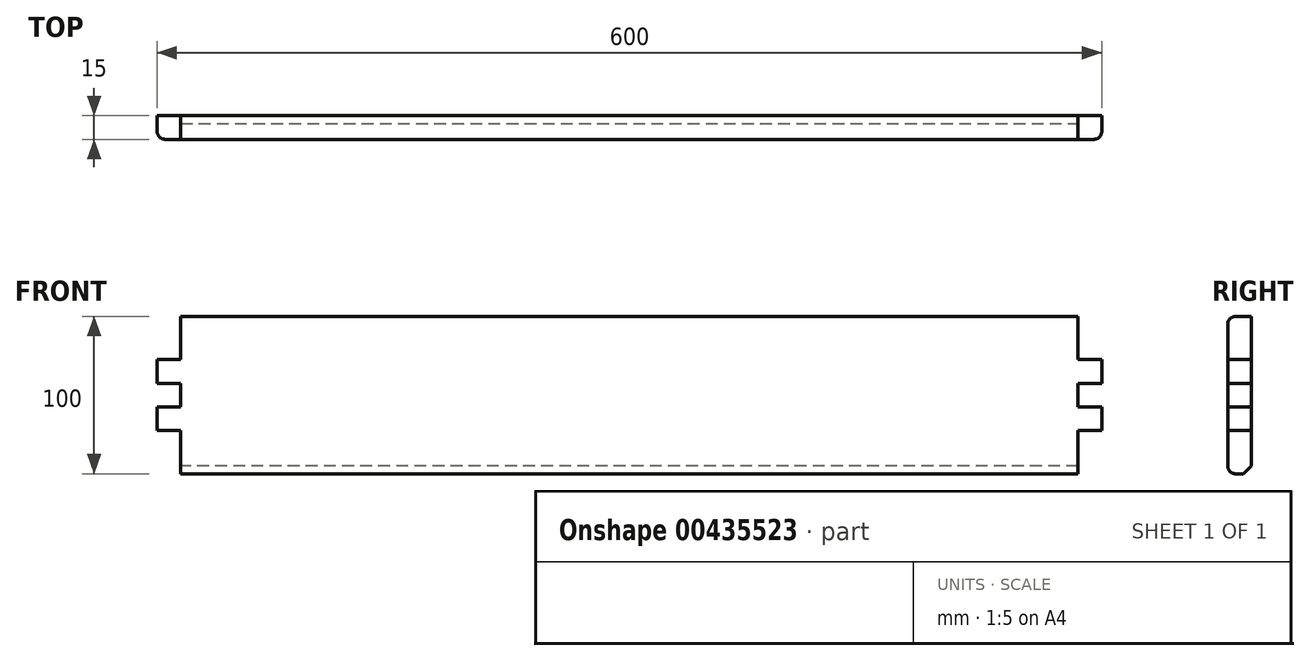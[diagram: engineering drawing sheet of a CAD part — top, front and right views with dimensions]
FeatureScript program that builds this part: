
annotation { "Feature Type Name" : "Feature", "Feature Type Description" : "" }
export const myFeature = defineFeature(function(context is Context, id is Id, definition is map)
    precondition{}
    {
        {
            var Q0;
            Q0=qCreatedBy(makeId("Front.planeOp"),FACE);
            var sketch = newSketch(context, id + "F0", { "sketchPlane" : qUnion([Q0])});
            skPoint(sketch, "E0.middle", {"position": v(0, 0) * mm});
            skLineSegment(sketch, "E1", {"start": v(-285, -22.5) * mm, "end": v(-300, -22.5) * mm});
            skLineSegment(sketch, "E2", {"start": v(-300, -22.5) * mm, "end": v(-300, -7.5) * mm});
            skLineSegment(sketch, "E3", {"start": v(-300, -7.5) * mm, "end": v(-285, -7.5) * mm});
            skLineSegment(sketch, "E4", {"start": v(-285, 7.5) * mm, "end": v(-300, 7.5) * mm});
            skLineSegment(sketch, "E5", {"start": v(-300, 7.5) * mm, "end": v(-300, 22.5) * mm});
            skLineSegment(sketch, "E6", {"start": v(-300, 22.5) * mm, "end": v(-285, 22.5) * mm});
            skLineSegment(sketch, "E7", {"start": v(-285, 50) * mm, "end": v(-285, 22.5) * mm});
            skLineSegment(sketch, "E8", {"start": v(-285, 7.5) * mm, "end": v(-285, -7.5) * mm});
            skLineSegment(sketch, "E9", {"start": v(-285, -22.5) * mm, "end": v(-285, -50) * mm});
            skLineSegment(sketch, "E10", {"start": v(-285, 50) * mm, "end": v(0, 50) * mm});
            skLineSegment(sketch, "E11", {"start": v(0, -50) * mm, "end": v(-285, -50) * mm});
            skLineSegment(sketch, "E12.MirrorCS", {"start": v(285, 7.5) * mm, "end": v(300, 7.5) * mm});
            skLineSegment(sketch, "E13.MirrorCS", {"start": v(300, -7.5) * mm, "end": v(285, -7.5) * mm});
            skLineSegment(sketch, "E14.MirrorCS", {"start": v(285, -22.5) * mm, "end": v(300, -22.5) * mm});
            skLineSegment(sketch, "E15.MirrorCS", {"start": v(300, 7.5) * mm, "end": v(300, 22.5) * mm});
            skLineSegment(sketch, "E16.MirrorCS", {"start": v(300, -22.5) * mm, "end": v(300, -7.5) * mm});
            skLineSegment(sketch, "E17.MirrorCS", {"start": v(300, 22.5) * mm, "end": v(285, 22.5) * mm});
            skLineSegment(sketch, "E18.MirrorCS", {"start": v(285, 7.5) * mm, "end": v(285, -7.5) * mm});
            skLineSegment(sketch, "E19.MirrorCS", {"start": v(0, -50) * mm, "end": v(285, -50) * mm});
            skLineSegment(sketch, "E20.MirrorCS", {"start": v(285, 50) * mm, "end": v(0, 50) * mm});
            skLineSegment(sketch, "E21.MirrorCS", {"start": v(285, -22.5) * mm, "end": v(285, -50) * mm});
            skLineSegment(sketch, "E22.MirrorCS", {"start": v(285, 50) * mm, "end": v(285, 22.5) * mm});
            skSolve(sketch);
        }
        {
            var Q0;
            Q0=makeQuery(id+"F0.imprint","IMPRINT",FACE,{"disambiguationData":[TD([[makeQuery(id+"F0.imprint","IMPRINT",EDGE,{"derivedFrom":sQuery(id+"F0.wireOp",EDGE,"E1")}),-1.0]])]});
            extrude(context, id + "F1", {"entities" : qUnion([Q0]), "depth" : 15 * mm});
        }
        {
            var Q0;
            Q0=makeQuery(id+"F1.opExtrude","CAP_EDGE",EDGE,{"disambiguationData":[OSD([sQuery(id+"F0.wireOp",EDGE,"E15.MirrorCS")])],"isStart":false});
            var Q1;
            Q1=makeQuery(id+"F1.opExtrude","CAP_EDGE",EDGE,{"disambiguationData":[OSD([sQuery(id+"F0.wireOp",EDGE,"E16.MirrorCS")])],"isStart":false});
            var Q2;
            Q2=makeQuery(id+"F1.opExtrude","CAP_EDGE",EDGE,{"disambiguationData":[OSD([sQuery(id+"F0.wireOp",EDGE,"E2")])],"isStart":false});
            var Q3;
            Q3=makeQuery(id+"F1.opExtrude","CAP_EDGE",EDGE,{"disambiguationData":[OSD([sQuery(id+"F0.wireOp",EDGE,"E5")])],"isStart":false});
            fillet(context, id + "F2", {"entities" : qUnion([Q0, Q1, Q2, Q3]), "radius" : 5 * mm, "tangentPropagation" : true, "allowEdgeOverflow" : false});
        }
        {
            var Q0;
            Q0=makeQuery(id+"F1.opExtrude","CAP_EDGE",EDGE,{"disambiguationData":[OSD([sQuery(id+"F0.wireOp",EDGE,"E10"),sQuery(id+"F0.wireOp",EDGE,"E20.MirrorCS")])],"isStart":false});
            var Q1;
            Q1=makeQuery(id+"F1.opExtrude","CAP_EDGE",EDGE,{"disambiguationData":[OSD([sQuery(id+"F0.wireOp",EDGE,"E11"),sQuery(id+"F0.wireOp",EDGE,"E19.MirrorCS")])],"isStart":false});
            fillet(context, id + "F3", {"entities" : qUnion([Q0, Q1]), "radius" : 5 * mm, "tangentPropagation" : true, "allowEdgeOverflow" : false});
        }
        {
            var Q0;
            Q0=makeQuery(id+"F1.opExtrude","CAP_EDGE",EDGE,{"disambiguationData":[OSD([sQuery(id+"F0.wireOp",EDGE,"E11"),sQuery(id+"F0.wireOp",EDGE,"E19.MirrorCS")])],"isStart":true});
            chamfer(context, id + "F4", {"entities" : qUnion([Q0]), "width" : 5 * mm, "tangentPropagation" : true});
        }
    });
